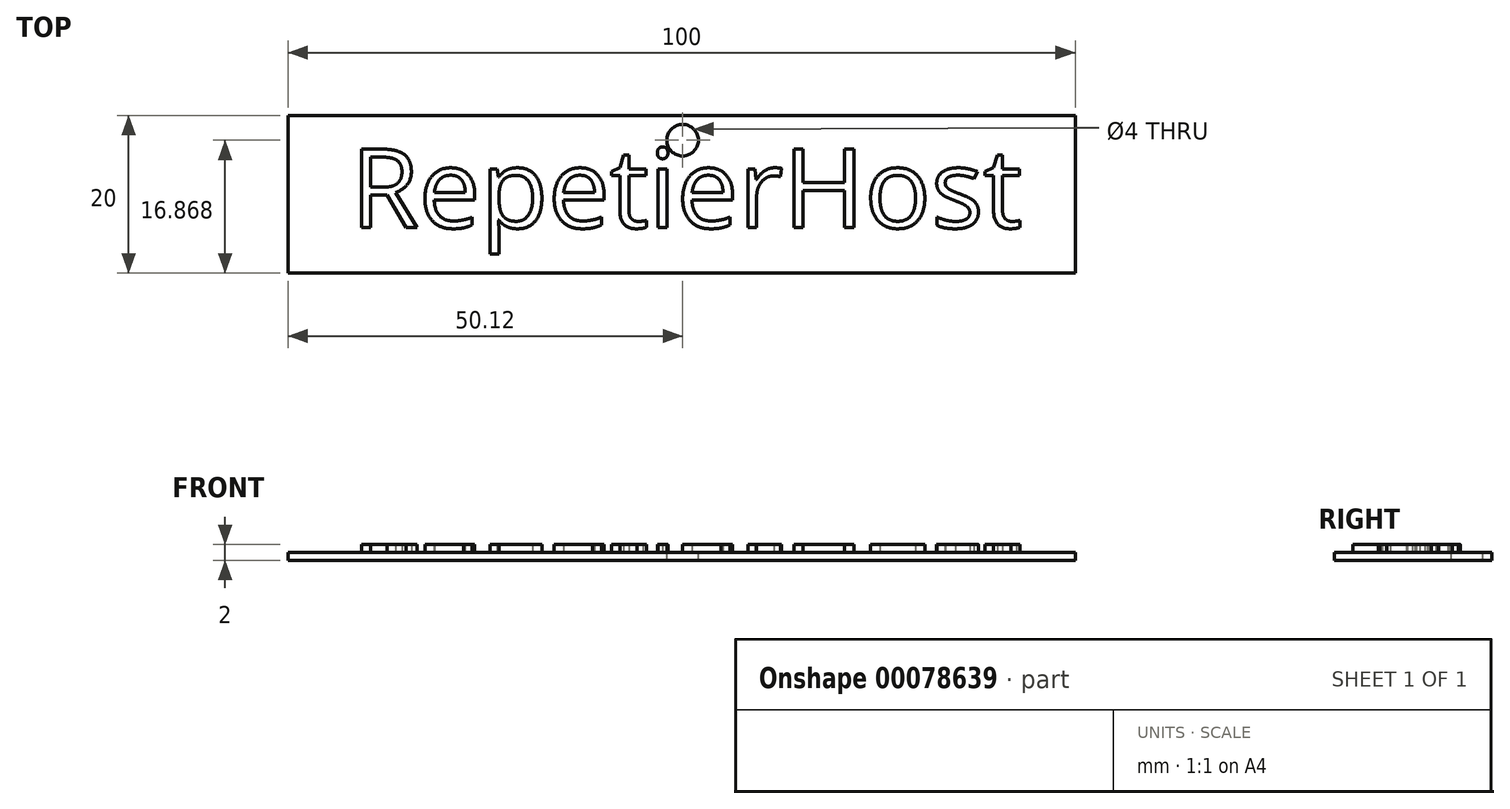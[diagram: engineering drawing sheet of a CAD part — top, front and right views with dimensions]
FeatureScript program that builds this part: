
annotation { "Feature Type Name" : "Feature", "Feature Type Description" : "" }
export const myFeature = defineFeature(function(context is Context, id is Id, definition is map)
    precondition{}
    {
        {
            var Q0;
            Q0=qCreatedBy(makeId("Top.planeOp"),FACE);
            var sketch = newSketch(context, id + "F0", { "sketchPlane" : qUnion([Q0])});
            skLineSegment(sketch, "E0.bottom", {"start": v(-50, -10) * mm, "end": v(50, -10) * mm});
            skLineSegment(sketch, "E0.top", {"start": v(-50, 10) * mm, "end": v(50, 10) * mm});
            skLineSegment(sketch, "E0.left", {"start": v(-50, -10) * mm, "end": v(-50, 10) * mm});
            skLineSegment(sketch, "E0.right", {"start": v(50, -10) * mm, "end": v(50, 10) * mm});
            skPoint(sketch, "E0.middle", {"position": v(0, 0) * mm});
            skSolve(sketch);
        }
        {
            var Q0;
            Q0=makeQuery(id+"F0.imprint","IMPRINT",FACE,{"disambiguationData":[TD([[makeQuery(id+"F0.imprint","IMPRINT",EDGE,{"derivedFrom":sQuery(id+"F0.wireOp",EDGE,"E0.bottom")}),1.0]])]});
            extrude(context, id + "F1", {"entities" : qUnion([Q0]), "depth" : 1 * mm});
        }
        {
            var Q0;
            Q0=makeQuery(id+"F1.opExtrude","CAP_FACE",FACE,{"disambiguationData":[OSD([sQuery(id+"F0.wireOp",EDGE,"E0.bottom"),sQuery(id+"F0.wireOp",EDGE,"E0.top"),sQuery(id+"F0.wireOp",EDGE,"E0.left"),sQuery(id+"F0.wireOp",EDGE,"E0.right")])],"isStart":false});
            var sketch = newSketch(context, id + "F2", { "sketchPlane" : qUnion([Q0])});
            skText(sketch, "E1", { "text": "RepetierHost", "fontName": "OpenSans-Regular.ttf"});
            const initialGuessF2  = {"E1": [-0.04204, -0.00425, 1, 0, 0.01007]};
            skSetInitialGuess(sketch, initialGuessF2);
            skSolve(sketch);
        }
        {
            var Q0;
            Q0 = qSketchRegion(id + "F2", true);
            extrude(context, id + "F3", {"entities" : qUnion([Q0]), "operationType" : NewBodyOperationType.ADD, "depth" : 1 * mm});
        }
        {
            var Q0;
            {var subQ0=sQuery(id+"F0.wireOp",EDGE,"E0.left");var subQ1=sQuery(id+"F0.wireOp",EDGE,"E0.bottom");var subQ2=sQuery(id+"F0.wireOp",EDGE,"E0.right");var subQ3=sQuery(id+"F0.wireOp",EDGE,"E0.top");Q0=makeQuery(id+"F3.boolean.opBoolean","SPLIT",FACE,{"disambiguationData":[TD([makeQuery(id+"F1.opExtrude","SWEPT_FACE",FACE,{"disambiguationData":[OSD([subQ1])]})])],"derivedFrom":makeQuery(id+"F1.opExtrude","CAP_FACE",FACE,{"disambiguationData":[OSD([subQ1,subQ3,subQ0,subQ2])],"isStart":false})});}
            var sketch = newSketch(context, id + "F4", { "sketchPlane" : qUnion([Q0])});
            skLineSegment(sketch, "E2", {"start": v(-50, 0) * mm, "end": v(50, -0.24) * mm, "construction": true});
            skLineSegment(sketch, "E3", {"start": v(-50, 10) * mm, "end": v(50, -10) * mm, "construction": true});
            skLineSegment(sketch, "E4", {"start": v(50, -10) * mm, "end": v(50, 10) * mm, "construction": true});
            skLineSegment(sketch, "E5", {"start": v(50, 10) * mm, "end": v(-50, -10) * mm, "construction": true});
            skLineSegment(sketch, "E6", {"start": v(-50, -10) * mm, "end": v(-50, 10) * mm, "construction": true});
            skLineSegment(sketch, "E7", {"start": v(0.12, -10) * mm, "end": v(0.12, 10) * mm, "construction": true});
            skPoint(sketch, "E8", {"position": v(0.12, 6.87) * mm});
            skSolve(sketch);
        }
        {
            var Q0;
            Q0=sQuery(id+"F4.wireOp",VERTEX,"E8");
            var Q1;
            Q1=makeQuery(id+"F1.opExtrude","SWEPT_BODY",BODY,{"disambiguationData":[OSD([sQuery(id+"F0.wireOp",EDGE,"E0.bottom"),sQuery(id+"F0.wireOp",EDGE,"E0.top"),sQuery(id+"F0.wireOp",EDGE,"E0.left"),sQuery(id+"F0.wireOp",EDGE,"E0.right")])]});
            hole(context, id + "F5", {"style" : HoleStyle.SIMPLE, "endStyle" : HoleEndStyle.BLIND, "holeDiameter" : 4 * mm, "holeDepth" : 50 * mm, "locations" : qUnion([Q0]), "scope" : qUnion([Q1])});
        }
    });
